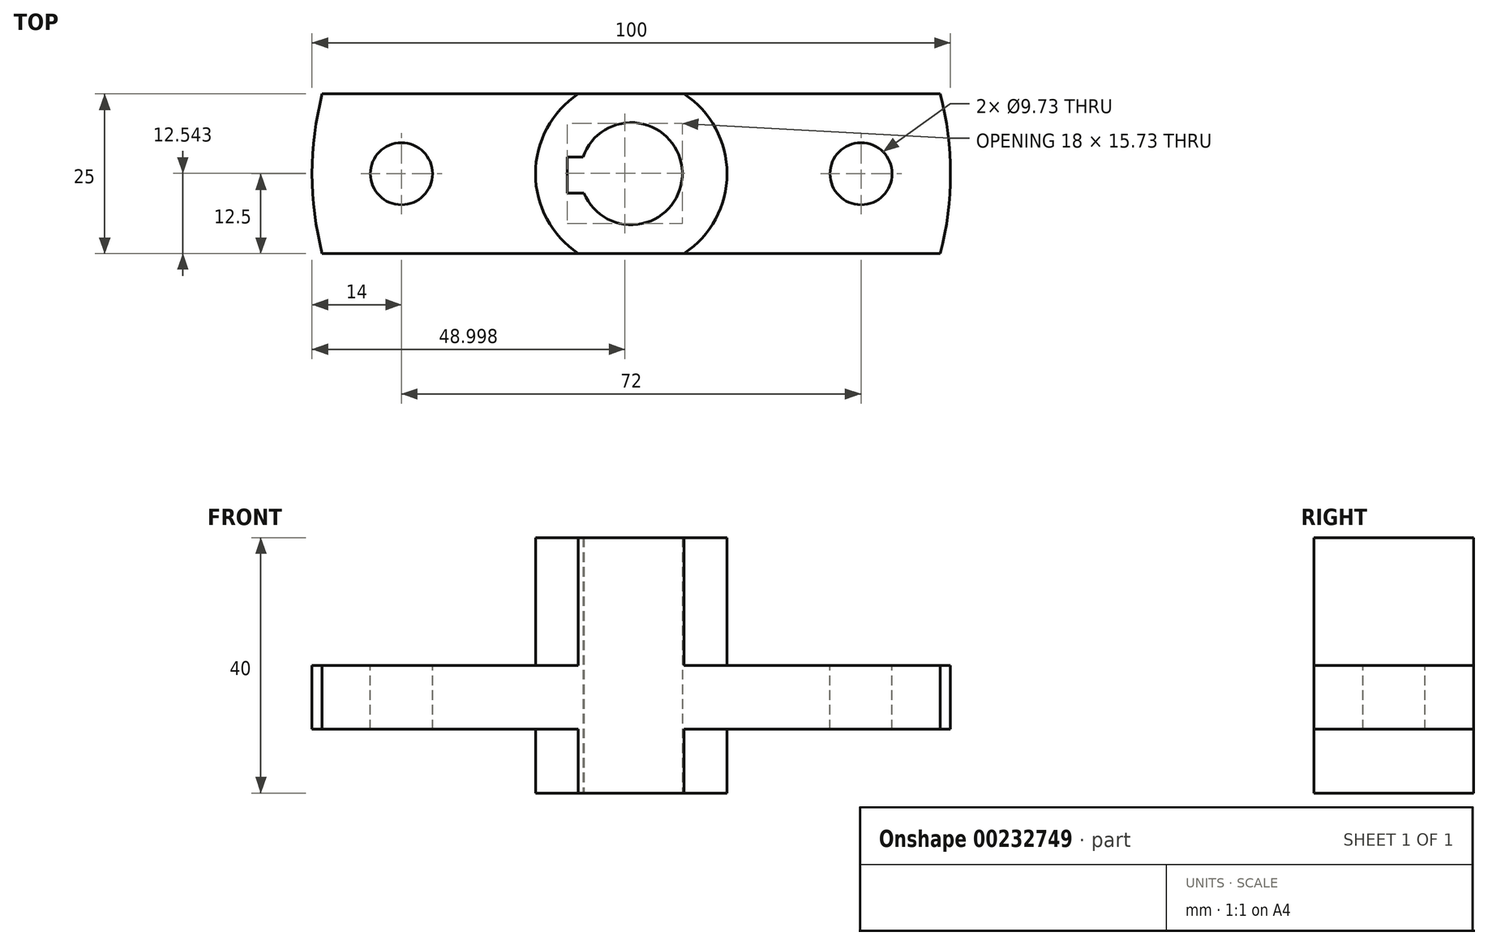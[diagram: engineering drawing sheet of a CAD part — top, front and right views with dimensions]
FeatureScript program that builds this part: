
annotation { "Feature Type Name" : "Feature", "Feature Type Description" : "" }
export const myFeature = defineFeature(function(context is Context, id is Id, definition is map)
    precondition{}
    {
        {
            var Q0;
            Q0=qCreatedBy(makeId("Top.planeOp"),FACE);
            var sketch = newSketch(context, id + "F0", { "sketchPlane" : qUnion([Q0])});
            skArc(sketch, "E0", {"start": v(-48.41, 12.5) * mm, "mid": v(-50, 0) * mm, "end": v(-48.41, -12.5) * mm});
            skLineSegment(sketch, "E1.bottom", {"start": v(48.41, 12.5) * mm, "end": v(-48.41, 12.5) * mm});
            skLineSegment(sketch, "E1.top", {"start": v(48.41, -12.5) * mm, "end": v(-48.41, -12.5) * mm});
            skArc(sketch, "E2", {"start": v(8.3, -12.5) * mm, "mid": v(15, 0) * mm, "end": v(8.3, 12.5) * mm});
            skArc(sketch, "E3", {"start": v(-7.4, -3.05) * mm, "mid": v(8, 0.24) * mm, "end": v(-7.56, 2.6) * mm});
            skLineSegment(sketch, "E4", {"start": v(-10, 2.6) * mm, "end": v(-10, -3.05) * mm});
            skLineSegment(sketch, "E5", {"start": v(-10, -3.05) * mm, "end": v(-7.4, -3.05) * mm});
            skLineSegment(sketch, "E6", {"start": v(-10, 2.6) * mm, "end": v(-7.56, 2.6) * mm});
            skArc(sketch, "E7.trimOffspring", {"start": v(48.41, -12.5) * mm, "mid": v(50, 0) * mm, "end": v(48.41, 12.5) * mm});
            skArc(sketch, "E8.trimOffspring", {"start": v(-8.3, 12.5) * mm, "mid": v(-15, 0) * mm, "end": v(-8.3, -12.5) * mm});
            skCircle(sketch, "E9", {"center": v(-36, 0) * mm, "radius": 4.87 * mm});
            skCircle(sketch, "E10", {"center": v(36, 0) * mm, "radius": 4.87 * mm});
            skSolve(sketch);
        }
        {
            var Q0;
            {var subQ0=sQuery(id+"F0.wireOp",EDGE,"E2");Q0=makeQuery(id+"F0.imprint","IMPRINT",FACE,{"disambiguationData":[TD([[makeQuery(id+"F0.imprint","IMPRINT",EDGE,{"derivedFrom":subQ0}),1.0]])]});}
            extrude(context, id + "F1", {"entities" : qUnion([Q0]), "endBound" : BoundingType.SYMMETRIC, "depth" : 40 * mm});
        }
        {
            var Q0;
            Q0 = qSketchRegion(id + "F0", true);
            extrude(context, id + "F2", {"entities" : qUnion([Q0]), "operationType" : NewBodyOperationType.ADD, "oppositeDirection" : true, "depth" : 10 * mm});
        }
    });
